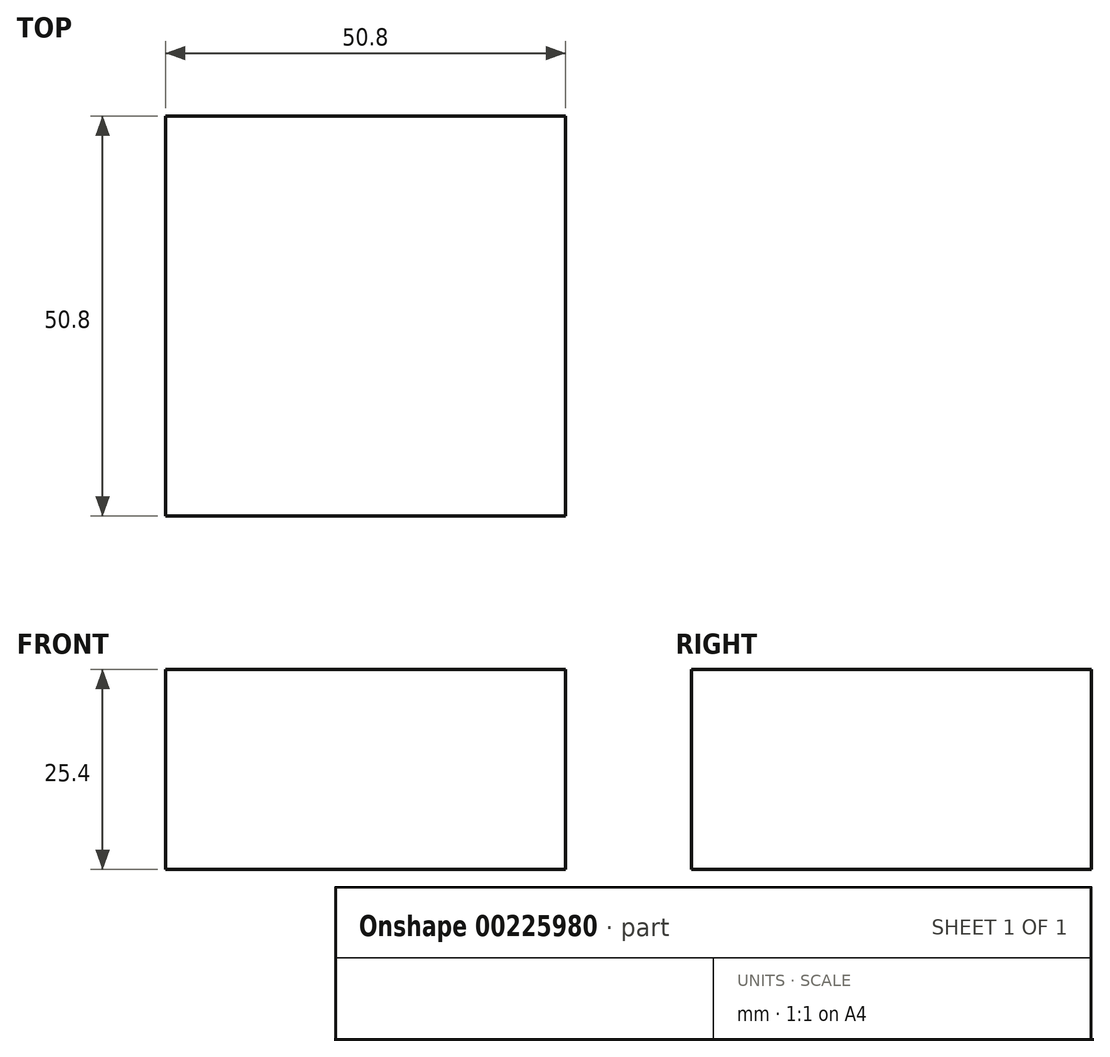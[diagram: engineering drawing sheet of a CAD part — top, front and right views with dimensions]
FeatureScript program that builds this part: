
annotation { "Feature Type Name" : "Feature", "Feature Type Description" : "" }
export const myFeature = defineFeature(function(context is Context, id is Id, definition is map)
    precondition{}
    {
        {
            var Q0;
            Q0=qCreatedBy(makeId("Front.planeOp"),FACE);
            var sketch = newSketch(context, id + "F0", { "sketchPlane" : qUnion([Q0])});
            skLineSegment(sketch, "E0.bottom", {"start": v(0, 0) * mm, "end": v(50.8, 0) * mm});
            skLineSegment(sketch, "E0.top", {"start": v(0, 25.4) * mm, "end": v(50.8, 25.4) * mm});
            skLineSegment(sketch, "E0.left", {"start": v(0, 0) * mm, "end": v(0, 25.4) * mm});
            skLineSegment(sketch, "E0.right", {"start": v(50.8, 0) * mm, "end": v(50.8, 25.4) * mm});
            skSolve(sketch);
        }
        {
            var Q0;
            Q0=makeQuery(id+"F0.imprint","IMPRINT",FACE,{"disambiguationData":[TD([[makeQuery(id+"F0.imprint","IMPRINT",EDGE,{"derivedFrom":sQuery(id+"F0.wireOp",EDGE,"E0.bottom")}),1.0]])]});
            extrude(context, id + "F1", {"entities" : qUnion([Q0]), "oppositeDirection" : true, "depth" : 50.8 * mm});
        }
    });
